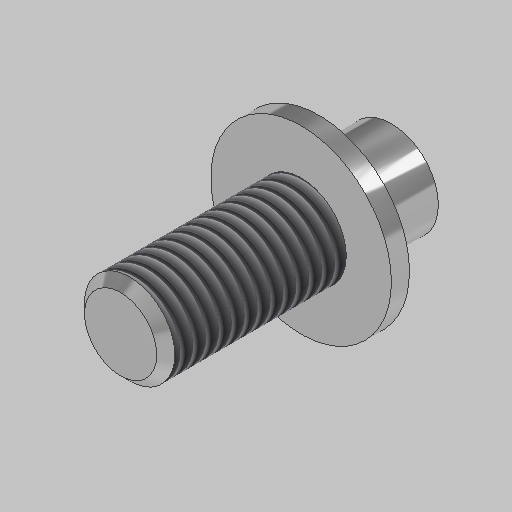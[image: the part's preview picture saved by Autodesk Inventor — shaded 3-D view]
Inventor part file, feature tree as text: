
AUTODESK INVENTOR PART (.ipt)
format: ipt  version: 2023.5 (Build 275446000, 446)  size: 179,712 bytes
history: native  units: mm (DEFAULTED — no unit token found)
features: extrude x3, chamfer x1, thread x1
ambient origin geometry x8: Origin, YZ Plane, XZ Plane, XY Plane, X Axis, Y Axis, Z Axis, Center Point
bodies: Solid1 (feature_tree)
feature tree (5):
  extrude  "Extrusion1"  Depth=12.7mm
  extrude  "Extrusion2"  Depth=1.27mm TaperAngle=0.0deg
  chamfer  "Chamfer1"  Distance=6.35mm
  thread  "Thread1"  [1 undecoded]
  extrude  "Extrusion3"  Depth=0.635mm
note: 1 required parameter value undecoded (feature->parameter linkage not recoverable at this tier; creation-order binding heuristic only, values carry confidence <= 0.55)
